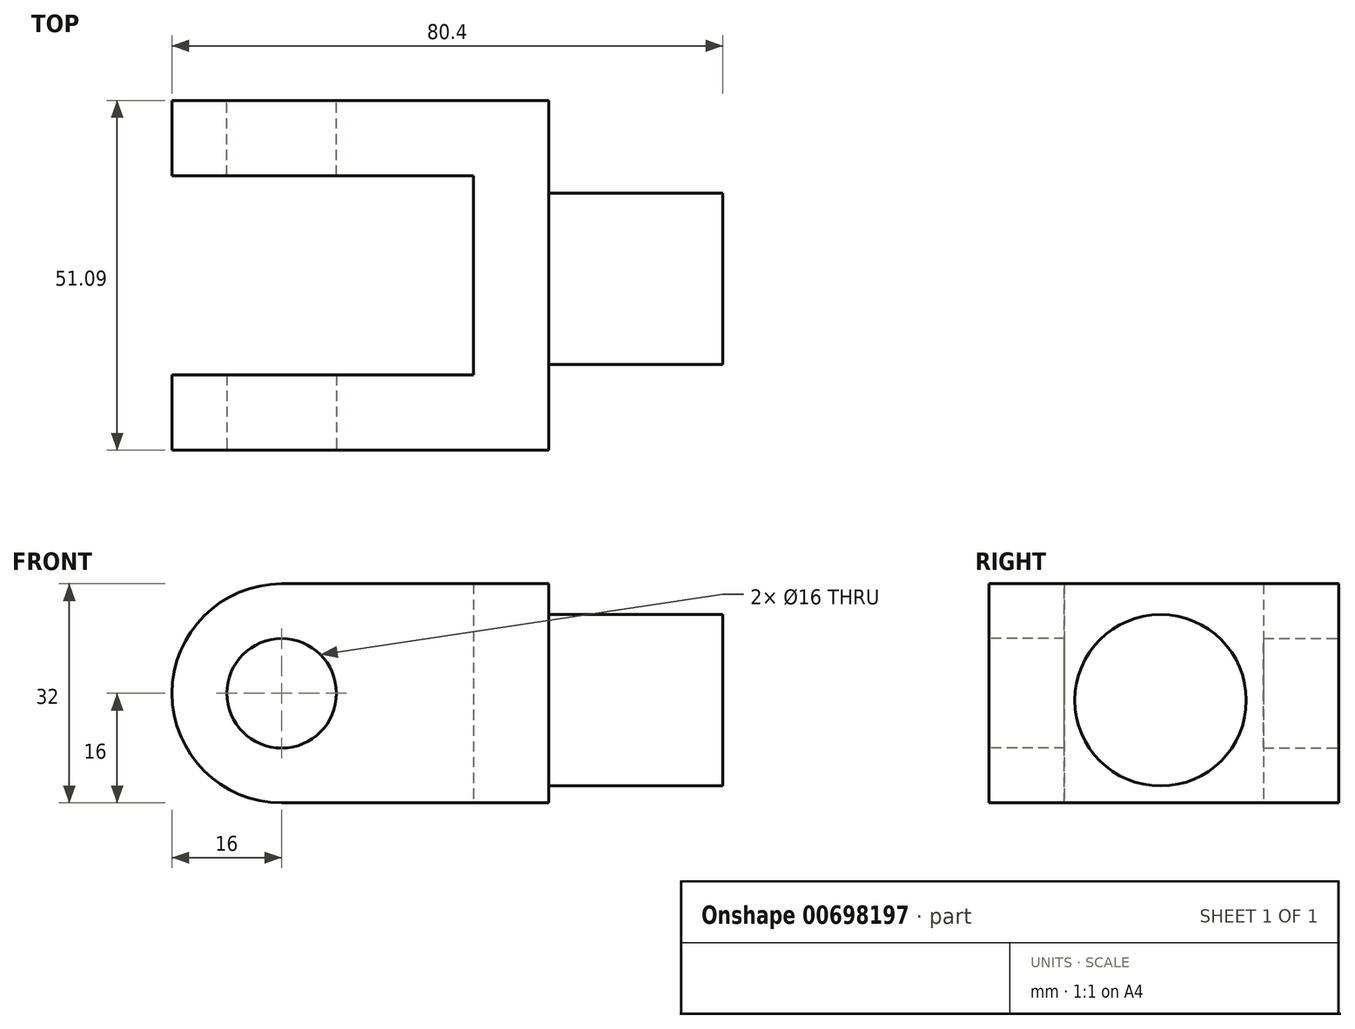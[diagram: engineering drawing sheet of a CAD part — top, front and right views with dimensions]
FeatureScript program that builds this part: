
annotation { "Feature Type Name" : "Feature", "Feature Type Description" : "" }
export const myFeature = defineFeature(function(context is Context, id is Id, definition is map)
    precondition{}
    {
        {
            var Q0;
            Q0=qCreatedBy(makeId("Top.planeOp"),FACE);
            var sketch = newSketch(context, id + "F0", { "sketchPlane" : qUnion([Q0])});
            skLineSegment(sketch, "E0", {"start": v(55, 19.98) * mm, "end": v(55, -31.1) * mm});
            skLineSegment(sketch, "E1", {"start": v(55, -31.1) * mm, "end": v(0, -31.1) * mm});
            skLineSegment(sketch, "E2", {"start": v(0, -31.1) * mm, "end": v(0, -20.1) * mm});
            skLineSegment(sketch, "E3", {"start": v(0, -20.1) * mm, "end": v(44, -20.1) * mm});
            skLineSegment(sketch, "E4", {"start": v(44, -20.1) * mm, "end": v(44, 8.98) * mm});
            skLineSegment(sketch, "E5", {"start": v(44, 8.98) * mm, "end": v(0, 8.98) * mm});
            skLineSegment(sketch, "E6", {"start": v(0, 8.98) * mm, "end": v(0, 19.98) * mm});
            skLineSegment(sketch, "E7", {"start": v(0, 19.98) * mm, "end": v(55, 19.98) * mm});
            skSolve(sketch);
        }
        {
            var Q0;
            Q0 = qSketchRegion(id + "F0", true);
            extrude(context, id + "F1", {"entities" : qUnion([Q0]), "depth" : 32 * mm, "offsetDistance" : 25.4 * mm});
        }
        {
            var Q0;
            Q0=makeQuery(id+"F1.opExtrude","CAP_EDGE",EDGE,{"disambiguationData":[OSD([sQuery(id+"F0.wireOp",EDGE,"E2")])],"isStart":false});
            fillet(context, id + "F2", {"entities" : qUnion([Q0]), "radius" : 16 * mm, "tangentPropagation" : true, "allowEdgeOverflow" : false});
        }
        {
            var Q0;
            Q0=makeQuery(id+"F1.opExtrude","CAP_EDGE",EDGE,{"disambiguationData":[OSD([sQuery(id+"F0.wireOp",EDGE,"E2")])],"isStart":true});
            fillet(context, id + "F3", {"entities" : qUnion([Q0]), "radius" : 16 * mm, "tangentPropagation" : true, "allowEdgeOverflow" : false});
        }
        {
            var Q0;
            Q0=makeQuery(id+"F1.opExtrude","CAP_EDGE",EDGE,{"disambiguationData":[OSD([sQuery(id+"F0.wireOp",EDGE,"E6")])],"isStart":false});
            fillet(context, id + "F4", {"entities" : qUnion([Q0]), "radius" : 16 * mm, "tangentPropagation" : true, "allowEdgeOverflow" : false});
        }
        {
            var Q0;
            Q0=makeQuery(id+"F1.opExtrude","CAP_EDGE",EDGE,{"disambiguationData":[OSD([sQuery(id+"F0.wireOp",EDGE,"E6")])],"isStart":true});
            fillet(context, id + "F5", {"entities" : qUnion([Q0]), "radius" : 16 * mm, "tangentPropagation" : true, "allowEdgeOverflow" : false});
        }
        {
            var Q0;
            Q0=makeQuery(id+"F1.opExtrude","SWEPT_FACE",FACE,{"disambiguationData":[OSD([sQuery(id+"F0.wireOp",EDGE,"E7")])]});
            var sketch = newSketch(context, id + "F6", { "sketchPlane" : qUnion([Q0])});
            skCircle(sketch, "E8", {"center": v(-16, 16) * mm, "radius": 8 * mm});
            skSolve(sketch);
        }
        {
            var Q0;
            Q0 = qSketchRegion(id + "F6", true);
            extrude(context, id + "F7", {"entities" : qUnion([Q0]), "operationType" : NewBodyOperationType.REMOVE, "oppositeDirection" : true, "depth" : 25.4 * mm, "offsetDistance" : 25.4 * mm});
        }
        {
            var Q0;
            Q0=makeQuery(id+"F1.opExtrude","SWEPT_FACE",FACE,{"disambiguationData":[OSD([sQuery(id+"F0.wireOp",EDGE,"E1")])]});
            var sketch = newSketch(context, id + "F8", { "sketchPlane" : qUnion([Q0])});
            skCircle(sketch, "E9", {"center": v(16, 16) * mm, "radius": 8 * mm});
            skSolve(sketch);
        }
        {
            var Q0;
            Q0 = qSketchRegion(id + "F8", true);
            extrude(context, id + "F9", {"entities" : qUnion([Q0]), "operationType" : NewBodyOperationType.REMOVE, "oppositeDirection" : true, "depth" : 25.4 * mm, "offsetDistance" : 25.4 * mm});
        }
        {
            var Q0;
            Q0=makeQuery(id+"F1.opExtrude","SWEPT_FACE",FACE,{"disambiguationData":[OSD([sQuery(id+"F0.wireOp",EDGE,"E0")])]});
            var sketch = newSketch(context, id + "F10", { "sketchPlane" : qUnion([Q0])});
            skCircle(sketch, "E10", {"center": v(-6.06, 14.98) * mm, "radius": 12.5 * mm});
            skSolve(sketch);
        }
        {
            var Q0;
            Q0 = qSketchRegion(id + "F10", true);
            extrude(context, id + "F11", {"entities" : qUnion([Q0]), "operationType" : NewBodyOperationType.ADD, "depth" : 25.4 * mm, "offsetDistance" : 25.4 * mm});
        }
    });
